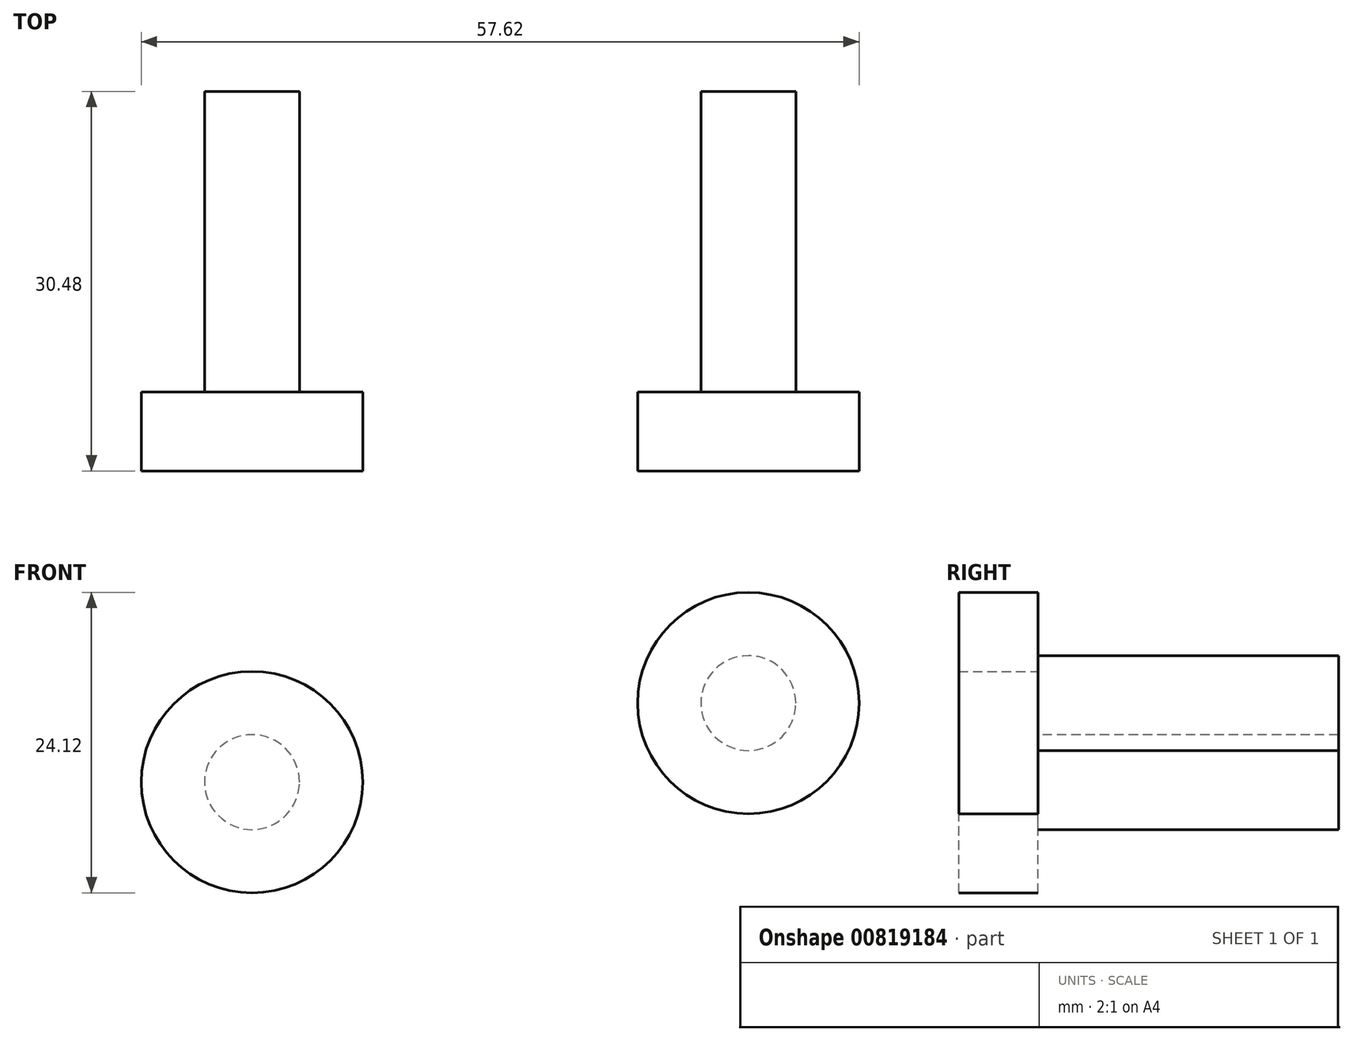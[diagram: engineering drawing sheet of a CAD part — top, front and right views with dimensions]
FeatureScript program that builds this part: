
annotation { "Feature Type Name" : "Feature", "Feature Type Description" : "" }
export const myFeature = defineFeature(function(context is Context, id is Id, definition is map)
    precondition{}
    {
        {
            var Q0;
            Q0=qCreatedBy(makeId("Front.planeOp"),FACE);
            var sketch = newSketch(context, id + "F0", { "sketchPlane" : qUnion([Q0])});
            skCircle(sketch, "E0", {"center": v(-52.12, 13.58) * mm, "radius": 8.9 * mm});
            skCircle(sketch, "E1", {"center": v(-12.28, 19.92) * mm, "radius": 8.9 * mm});
            skSolve(sketch);
        }
        {
            var Q0;
            Q0=makeQuery(id+"F0.imprint","IMPRINT",FACE,{"disambiguationData":[TD([[makeQuery(id+"F0.imprint","IMPRINT",EDGE,{"derivedFrom":sQuery(id+"F0.wireOp",EDGE,"E0")}),1.0]])]});
            var Q1;
            Q1=makeQuery(id+"F0.imprint","IMPRINT",FACE,{"disambiguationData":[TD([[makeQuery(id+"F0.imprint","IMPRINT",EDGE,{"derivedFrom":sQuery(id+"F0.wireOp",EDGE,"E1")}),1.0]])]});
            extrude(context, id + "F1", {"entities" : qUnion([Q0, Q1]), "depth" : 6.35 * mm, "offsetDistance" : 25.4 * mm});
        }
        {
            var Q0;
            Q0=qCreatedBy(makeId("Front.planeOp"),FACE);
            var sketch = newSketch(context, id + "F2", { "sketchPlane" : qUnion([Q0])});
            skCircle(sketch, "E2", {"center": v(-52.12, 13.58) * mm, "radius": 3.81 * mm});
            skCircle(sketch, "E3", {"center": v(-12.28, 19.92) * mm, "radius": 3.81 * mm});
            skSolve(sketch);
        }
        {
            var Q0;
            Q0 = qSketchRegion(id + "F2", true);
            extrude(context, id + "F3", {"entities" : qUnion([Q0]), "oppositeDirection" : true, "depth" : 24.13 * mm, "offsetDistance" : 25.4 * mm});
        }
    });
